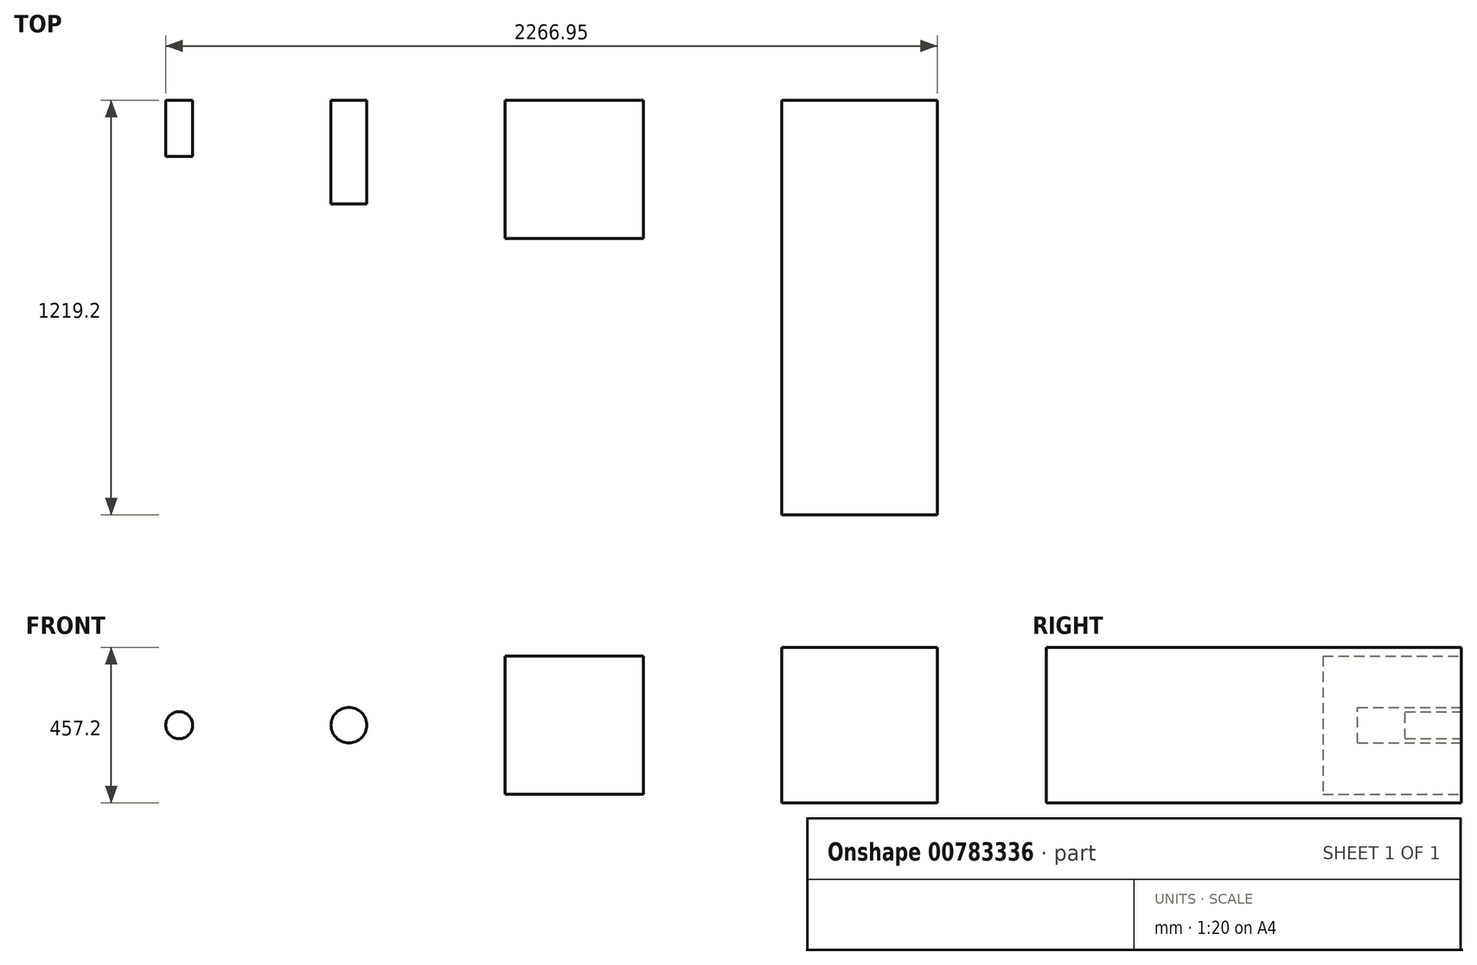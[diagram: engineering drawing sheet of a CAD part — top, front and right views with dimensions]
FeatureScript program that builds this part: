
annotation { "Feature Type Name" : "Feature", "Feature Type Description" : "" }
export const myFeature = defineFeature(function(context is Context, id is Id, definition is map)
    precondition{}
    {
        {
            var Q0;
            Q0=qCreatedBy(makeId("Front.planeOp"),FACE);
            var sketch = newSketch(context, id + "F0", { "sketchPlane" : qUnion([Q0])});
            skCircle(sketch, "E0", {"center": v(0, 0) * mm, "radius": 52.39 * mm});
            skSolve(sketch);
        }
        {
            var Q0;
            Q0 = qSketchRegion(id + "F0", true);
            extrude(context, id + "F1", {"entities" : qUnion([Q0]), "depth" : 304.8 * mm, "offsetDistance" : 25 * mm});
        }
        {
            var Q0;
            Q0=qCreatedBy(makeId("Front.planeOp"),FACE);
            var sketch = newSketch(context, id + "F2", { "sketchPlane" : qUnion([Q0])});
            skCircle(sketch, "E1", {"center": v(-498.48, 0) * mm, "radius": 39.69 * mm});
            skLineSegment(sketch, "E2", {"start": v(-52.39, 0) * mm, "end": v(-458.79, 0) * mm, "construction": true});
            skSolve(sketch);
        }
        {
            var Q0;
            Q0 = qSketchRegion(id + "F2", true);
            extrude(context, id + "F3", {"entities" : qUnion([Q0]), "depth" : 165.1 * mm, "offsetDistance" : 25 * mm});
        }
        {
            var Q0;
            Q0=qCreatedBy(makeId("Front.planeOp"),FACE);
            var sketch = newSketch(context, id + "F4", { "sketchPlane" : qUnion([Q0])});
            skLineSegment(sketch, "E3.bottom", {"start": v(458.79, 203.2) * mm, "end": v(865.19, 203.2) * mm});
            skLineSegment(sketch, "E3.top", {"start": v(458.79, -203.2) * mm, "end": v(865.19, -203.2) * mm});
            skLineSegment(sketch, "E3.left", {"start": v(458.79, 203.2) * mm, "end": v(458.79, -203.2) * mm});
            skLineSegment(sketch, "E3.right", {"start": v(865.19, 203.2) * mm, "end": v(865.19, -203.2) * mm});
            skLineSegment(sketch, "E4", {"start": v(-458.79, 0) * mm, "end": v(-52.39, 0) * mm, "construction": true});
            skLineSegment(sketch, "E5", {"start": v(52.39, 0) * mm, "end": v(458.79, 0) * mm, "construction": true});
            skLineSegment(sketch, "E6.bottom", {"start": v(1271.59, 228.6) * mm, "end": v(1728.79, 228.6) * mm});
            skLineSegment(sketch, "E6.top", {"start": v(1271.59, -228.6) * mm, "end": v(1728.79, -228.6) * mm});
            skLineSegment(sketch, "E6.left", {"start": v(1271.59, 228.6) * mm, "end": v(1271.59, -228.6) * mm});
            skLineSegment(sketch, "E6.right", {"start": v(1728.79, 228.6) * mm, "end": v(1728.79, -228.6) * mm});
            skLineSegment(sketch, "E7", {"start": v(865.19, 0) * mm, "end": v(1271.59, 0) * mm, "construction": true});
            skSolve(sketch);
        }
        {
            var Q0;
            Q0 = qSketchRegion(id + "F4", true);
            extrude(context, id + "F5", {"entities" : qUnion([Q0]), "depth" : 406.4 * mm, "offsetDistance" : 25 * mm});
        }
        {
            var Q0;
            Q0=makeQuery(id+"F5.opExtrude","CAP_FACE",FACE,{"disambiguationData":[OSD([sQuery(id+"F4.wireOp",EDGE,"E6.bottom"),sQuery(id+"F4.wireOp",EDGE,"E6.top"),sQuery(id+"F4.wireOp",EDGE,"E6.left"),sQuery(id+"F4.wireOp",EDGE,"E6.right")])],"isStart":false});
            var sketch = newSketch(context, id + "F6", { "sketchPlane" : qUnion([Q0])});
            skLineSegment(sketch, "E8.bottom", {"start": v(1271.59, 228.6) * mm, "end": v(1728.79, 228.6) * mm});
            skLineSegment(sketch, "E8.top", {"start": v(1271.59, -228.6) * mm, "end": v(1728.79, -228.6) * mm});
            skLineSegment(sketch, "E8.left", {"start": v(1271.59, 228.6) * mm, "end": v(1271.59, -228.6) * mm});
            skLineSegment(sketch, "E8.right", {"start": v(1728.79, 228.6) * mm, "end": v(1728.79, -228.6) * mm});
            skSolve(sketch);
        }
        {
            var Q0;
            Q0=makeQuery(id+"F6.imprint","IMPRINT",FACE,{"disambiguationData":[TD([[makeQuery(id+"F6.imprint","IMPRINT",EDGE,{"derivedFrom":sQuery(id+"F6.wireOp",EDGE,"E8.bottom")}),-1.0]])]});
            extrude(context, id + "F7", {"entities" : qUnion([Q0]), "operationType" : NewBodyOperationType.ADD, "depth" : 812.8 * mm, "offsetDistance" : 25 * mm});
        }
    });
